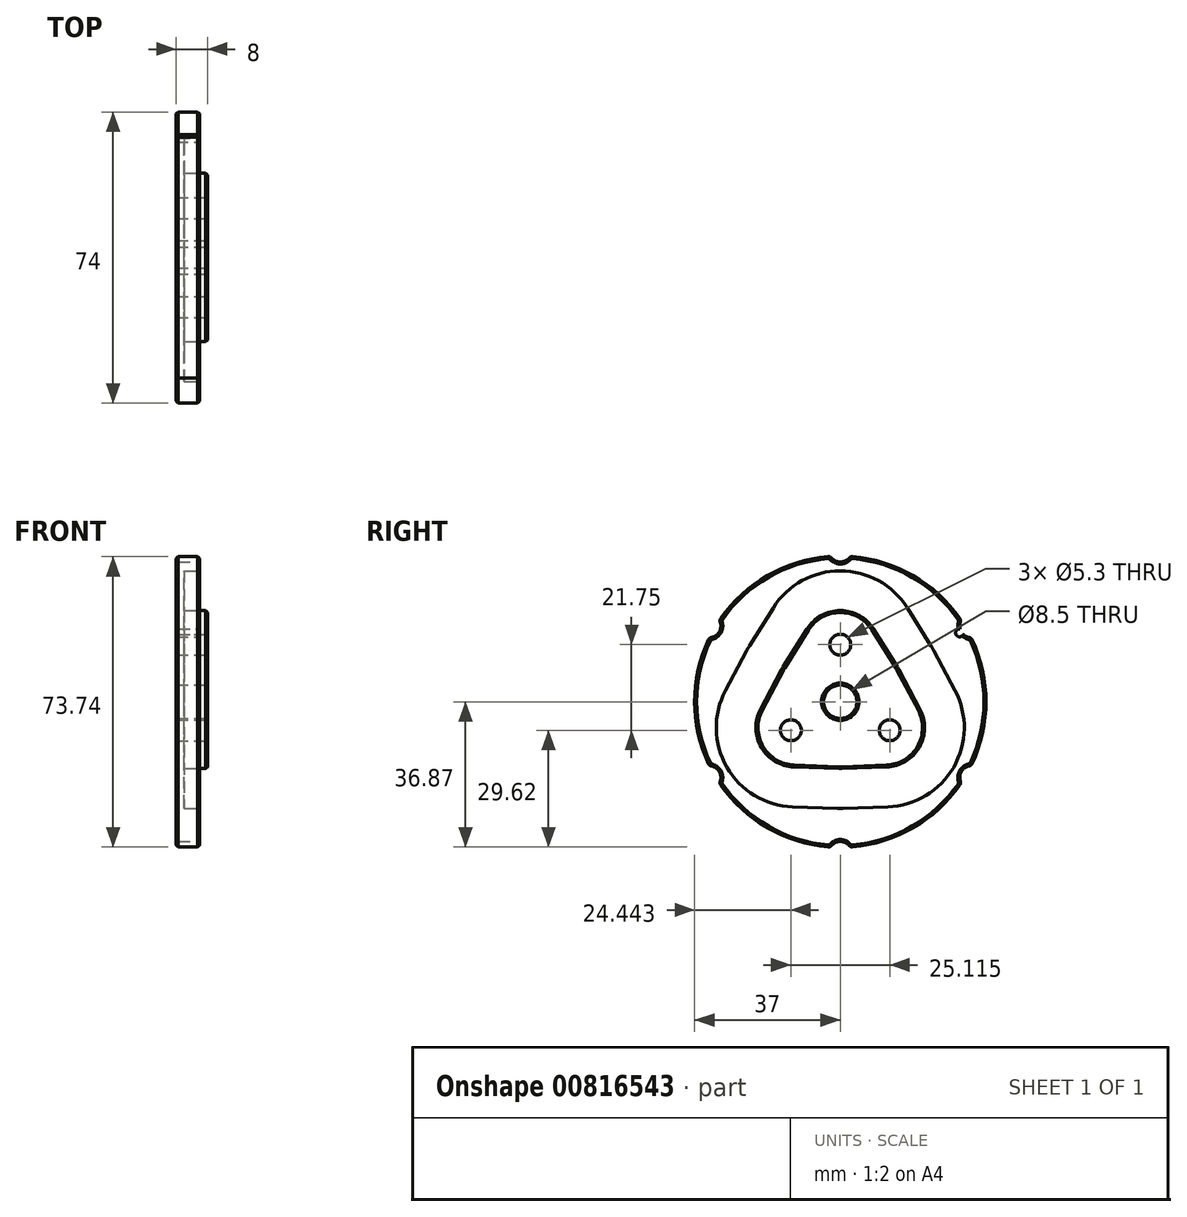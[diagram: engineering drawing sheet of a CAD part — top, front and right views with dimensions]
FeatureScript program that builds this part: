
annotation { "Feature Type Name" : "Feature", "Feature Type Description" : "" }
export const myFeature = defineFeature(function(context is Context, id is Id, definition is map)
    precondition{}
    {
        {
            var Q0;
            Q0=qCreatedBy(makeId("Right.planeOp"),FACE);
            var sketch = newSketch(context, id + "F0", { "sketchPlane" : qUnion([Q0])});
            skArc(sketch, "E0", {"start": v(-3.09, 36.87) * mm, "mid": v(-18.5, 32.04) * mm, "end": v(-30.39, 21.1) * mm});
            skCircle(sketch, "E1", {"center": v(0, 0) * mm, "radius": 4.25 * mm});
            skLineSegment(sketch, "E2", {"start": v(0, 50.53) * mm, "end": v(0, -45.3) * mm, "construction": true});
            skLineSegment(sketch, "E3", {"start": v(0, 0) * mm, "end": v(28.08, 48.64) * mm, "construction": true});
            skLineSegment(sketch, "E4", {"start": v(0, 0) * mm, "end": v(48.73, -28.13) * mm, "construction": true});
            skLineSegment(sketch, "E5.MirrorCS", {"start": v(0, 0) * mm, "end": v(-28.08, 48.64) * mm, "construction": true});
            skLineSegment(sketch, "E6.MirrorCS", {"start": v(-43.76, 25.27) * mm, "end": v(32.04, -18.5) * mm, "construction": true});
            skLineSegment(sketch, "E7.MirrorCS", {"start": v(0, 0) * mm, "end": v(-28.08, -48.64) * mm, "construction": true});
            skLineSegment(sketch, "E8.MirrorCS", {"start": v(0, 0) * mm, "end": v(28.08, -48.64) * mm, "construction": true});
            skLineSegment(sketch, "E9", {"start": v(-8.48, 18.48) * mm, "end": v(-14.54, 8.81) * mm});
            skLineSegment(sketch, "E10", {"start": v(-14.9, 8.18) * mm, "end": v(-20.25, -1.9) * mm});
            skLineSegment(sketch, "E11", {"start": v(-11.78, -16.58) * mm, "end": v(-0.36, -17) * mm});
            skLineSegment(sketch, "E12", {"start": v(0.36, -17) * mm, "end": v(11.77, -16.58) * mm});
            skLineSegment(sketch, "E13", {"start": v(20.24, -1.9) * mm, "end": v(14.9, 8.18) * mm});
            skLineSegment(sketch, "E14", {"start": v(14.53, 8.8) * mm, "end": v(8.47, 18.48) * mm});
            skPoint(sketch, "E15.visualSharp", {"position": v(0, 32) * mm});
            skArc(sketch, "E15.filletArc", {"start": v(8.47, 18.48) * mm, "mid": v(0, 23.17) * mm, "end": v(-8.48, 18.48) * mm});
            skPoint(sketch, "E16.visualSharp", {"position": v(-14.73, 8.5) * mm});
            skArc(sketch, "E16.filletArc", {"start": v(-14.54, 8.81) * mm, "mid": v(-14.73, 8.5) * mm, "end": v(-14.9, 8.18) * mm});
            skPoint(sketch, "E17.visualSharp", {"position": v(-27.71, -16) * mm});
            skArc(sketch, "E17.filletArc", {"start": v(-20.25, -1.9) * mm, "mid": v(-20.07, -11.59) * mm, "end": v(-11.78, -16.58) * mm});
            skPoint(sketch, "E18.visualSharp", {"position": v(0, -17.01) * mm});
            skArc(sketch, "E18.filletArc", {"start": v(-0.36, -17) * mm, "mid": v(0, -17) * mm, "end": v(0.36, -17) * mm});
            skPoint(sketch, "E19.visualSharp", {"position": v(27.71, -16) * mm});
            skArc(sketch, "E19.filletArc", {"start": v(11.77, -16.58) * mm, "mid": v(20.07, -11.59) * mm, "end": v(20.24, -1.9) * mm});
            skPoint(sketch, "E20.visualSharp", {"position": v(14.72, 8.5) * mm});
            skArc(sketch, "E20.filletArc", {"start": v(14.9, 8.18) * mm, "mid": v(14.72, 8.5) * mm, "end": v(14.53, 8.8) * mm});
            skLineSegment(sketch, "E21.0", {"start": v(-17.03, 23.85) * mm, "end": v(-23.1, 14.18) * mm});
            skArc(sketch, "E21.1", {"start": v(-0.73, -27.1) * mm, "mid": v(0, -27.1) * mm, "end": v(0.73, -27.1) * mm});
            skLineSegment(sketch, "E21.2", {"start": v(-12.14, -26.67) * mm, "end": v(-0.73, -27.1) * mm});
            skArc(sketch, "E21.3", {"start": v(-29.17, 2.82) * mm, "mid": v(-28.82, -16.64) * mm, "end": v(-12.14, -26.67) * mm});
            skLineSegment(sketch, "E21.4", {"start": v(-23.83, 12.91) * mm, "end": v(-29.17, 2.82) * mm});
            skLineSegment(sketch, "E21.5", {"start": v(0.73, -27.1) * mm, "end": v(12.14, -26.68) * mm});
            skArc(sketch, "E21.6", {"start": v(-23.1, 14.18) * mm, "mid": v(-23.47, 13.55) * mm, "end": v(-23.83, 12.91) * mm});
            skArc(sketch, "E21.7", {"start": v(12.14, -26.68) * mm, "mid": v(28.81, -16.63) * mm, "end": v(29.16, 2.83) * mm});
            skLineSegment(sketch, "E21.8", {"start": v(29.16, 2.83) * mm, "end": v(23.81, 12.91) * mm});
            skArc(sketch, "E21.9", {"start": v(23.81, 12.91) * mm, "mid": v(23.46, 13.55) * mm, "end": v(23.09, 14.17) * mm});
            skLineSegment(sketch, "E21.10", {"start": v(23.09, 14.17) * mm, "end": v(17.03, 23.84) * mm});
            skArc(sketch, "E21.11", {"start": v(17.03, 23.84) * mm, "mid": v(0, 33.27) * mm, "end": v(-17.03, 23.85) * mm});
            skCircle(sketch, "E22", {"center": v(0, 0) * mm, "radius": 14.5 * mm, "construction": true});
            skCircle(sketch, "E23", {"center": v(-12.56, -7.25) * mm, "radius": 2.65 * mm});
            skCircle(sketch, "E24", {"center": v(12.56, -7.25) * mm, "radius": 2.65 * mm});
            skCircle(sketch, "E25", {"center": v(0, 14.5) * mm, "radius": 2.65 * mm});
            skArc(sketch, "E26", {"start": v(30.45, 18.5) * mm, "mid": v(29.44, 17) * mm, "end": v(31.24, 17.13) * mm});
            skArc(sketch, "E27", {"start": v(-2.25, 36.53) * mm, "mid": v(0, 35.5) * mm, "end": v(2.25, 36.53) * mm});
            skPoint(sketch, "E28.visualSharp", {"position": v(-2.53, 36.91) * mm});
            skArc(sketch, "E28.filletArc", {"start": v(-2.25, 36.53) * mm, "mid": v(-2.63, 36.8) * mm, "end": v(-3.09, 36.87) * mm});
            skPoint(sketch, "E29.visualSharp", {"position": v(2.53, 36.91) * mm});
            skArc(sketch, "E29.filletArc", {"start": v(3.09, 36.87) * mm, "mid": v(2.63, 36.8) * mm, "end": v(2.25, 36.53) * mm});
            skPoint(sketch, "E30.center.orphan", {"position": v(0, -35) * mm});
            skArc(sketch, "E31.MirrorCS", {"start": v(32.76, 16.32) * mm, "mid": v(33.19, 16.12) * mm, "end": v(33.48, 15.76) * mm});
            skArc(sketch, "E32.MirrorCS", {"start": v(30.39, 21.1) * mm, "mid": v(30.56, 20.68) * mm, "end": v(30.51, 20.22) * mm});
            skPoint(sketch, "E33.MirrorP", {"position": v(33.23, 16.26) * mm});
            skArc(sketch, "E34.MirrorCS", {"start": v(32.76, 16.32) * mm, "mid": v(31.94, 16.6) * mm, "end": v(31.24, 17.13) * mm});
            skPoint(sketch, "E35.MirrorP", {"position": v(30.7, 20.65) * mm});
            skArc(sketch, "E36.trimOffspring", {"start": v(30.39, 21.1) * mm, "mid": v(18.5, 32.04) * mm, "end": v(3.09, 36.87) * mm});
            skLineSegment(sketch, "E37.trimOffspring", {"start": v(31.18, 18) * mm, "end": v(-39.22, -22.65) * mm, "construction": true});
            skArc(sketch, "E38.trimOffspring", {"start": v(30.45, 18.5) * mm, "mid": v(30.35, 19.36) * mm, "end": v(30.51, 20.22) * mm});
            skArc(sketch, "E39.MirrorCS", {"start": v(-30.51, 20.22) * mm, "mid": v(-30.56, 20.68) * mm, "end": v(-30.39, 21.1) * mm});
            skArc(sketch, "E40.MirrorCS", {"start": v(-33.48, 15.76) * mm, "mid": v(-33.19, 16.12) * mm, "end": v(-32.76, 16.32) * mm});
            skPoint(sketch, "E41.MirrorP", {"position": v(-33.23, 16.26) * mm});
            skPoint(sketch, "E42.MirrorP", {"position": v(-30.7, 20.65) * mm});
            skArc(sketch, "E43.MirrorCS", {"start": v(-30.51, 20.22) * mm, "mid": v(-30.75, 17.75) * mm, "end": v(-32.76, 16.32) * mm});
            skArc(sketch, "E44.trimOffspring", {"start": v(-33.48, 15.76) * mm, "mid": v(-37, 0) * mm, "end": v(-33.48, -15.76) * mm});
            skArc(sketch, "E45.MirrorCS", {"start": v(-33.48, -15.76) * mm, "mid": v(-33.19, -16.12) * mm, "end": v(-32.76, -16.32) * mm});
            skArc(sketch, "E46.MirrorCS", {"start": v(-30.51, -20.22) * mm, "mid": v(-30.56, -20.68) * mm, "end": v(-30.39, -21.1) * mm});
            skPoint(sketch, "E47.MirrorP", {"position": v(-30.7, -20.65) * mm});
            skArc(sketch, "E48.MirrorCS", {"start": v(-30.51, -20.22) * mm, "mid": v(-30.75, -17.75) * mm, "end": v(-32.76, -16.32) * mm});
            skPoint(sketch, "E49.MirrorP", {"position": v(-33.23, -16.26) * mm});
            skArc(sketch, "E50.trimOffspring", {"start": v(-30.39, -21.1) * mm, "mid": v(-18.5, -32.04) * mm, "end": v(-3.09, -36.87) * mm});
            skArc(sketch, "E51.MirrorCS", {"start": v(3.09, -36.87) * mm, "mid": v(2.63, -36.8) * mm, "end": v(2.25, -36.53) * mm});
            skArc(sketch, "E52.MirrorCS", {"start": v(-2.25, -36.53) * mm, "mid": v(-2.63, -36.8) * mm, "end": v(-3.09, -36.87) * mm});
            skArc(sketch, "E53.MirrorCS", {"start": v(-2.25, -36.53) * mm, "mid": v(0, -35.5) * mm, "end": v(2.25, -36.53) * mm});
            skPoint(sketch, "E54.MirrorP", {"position": v(-2.53, -36.91) * mm});
            skPoint(sketch, "E55.MirrorP", {"position": v(2.53, -36.91) * mm});
            skArc(sketch, "E56.trimOffspring", {"start": v(3.09, -36.87) * mm, "mid": v(18.5, -32.04) * mm, "end": v(30.39, -21.1) * mm});
            skPoint(sketch, "E57.orphan", {"position": v(39.22, -22.65) * mm});
            skPoint(sketch, "E58.MirrorCS.start.orphan", {"position": v(43.76, 25.27) * mm});
            skArc(sketch, "E59.MirrorCS", {"start": v(30.39, -21.1) * mm, "mid": v(30.56, -20.68) * mm, "end": v(30.51, -20.22) * mm});
            skArc(sketch, "E60.MirrorCS", {"start": v(32.76, -16.32) * mm, "mid": v(33.19, -16.12) * mm, "end": v(33.48, -15.76) * mm});
            skPoint(sketch, "E61.MirrorP", {"position": v(33.23, -16.26) * mm});
            skPoint(sketch, "E62.MirrorP", {"position": v(30.7, -20.65) * mm});
            skPoint(sketch, "E63.MirrorP", {"position": v(30.31, -17.5) * mm});
            skArc(sketch, "E64.MirrorCS", {"start": v(32.76, -16.32) * mm, "mid": v(30.75, -17.75) * mm, "end": v(30.51, -20.22) * mm});
            skArc(sketch, "E65.trimOffspring", {"start": v(33.48, -15.76) * mm, "mid": v(37, 0) * mm, "end": v(33.48, 15.76) * mm});
            skSolve(sketch);
        }
        {
            var Q0;
            Q0 = qSketchRegion(id + "F0", true);
            var Q1;
            Q1=makeQuery(id+"F0.imprint","IMPRINT",FACE,{"disambiguationData":[TD([[makeQuery(id+"F0.imprint","IMPRINT",EDGE,{"derivedFrom":sQuery(id+"F0.wireOp",EDGE,"E9")}),-1.0]])]});
            var Q2;
            Q2=makeQuery(id+"F0.imprint","IMPRINT",FACE,{"disambiguationData":[TD([[makeQuery(id+"F0.imprint","IMPRINT",EDGE,{"derivedFrom":sQuery(id+"F0.wireOp",EDGE,"E1")}),-1.0]])]});
            extrude(context, id + "F1", {"entities" : qUnion([Q0, Q1, Q2]), "oppositeDirection" : true, "depth" : 6 * mm, "offsetDistance" : 25 * mm});
        }
        {
            var Q0;
            Q0=makeQuery(id+"F0.imprint","IMPRINT",FACE,{"disambiguationData":[TD([[makeQuery(id+"F0.imprint","IMPRINT",EDGE,{"derivedFrom":sQuery(id+"F0.wireOp",EDGE,"E9")}),-1.0]])]});
            extrude(context, id + "F2", {"entities" : qUnion([Q0]), "operationType" : NewBodyOperationType.REMOVE, "oppositeDirection" : true, "depth" : 4 * mm, "offsetDistance" : 25 * mm});
        }
        {
            var Q0;
            {var subQ0=sQuery(id+"F0.wireOp",EDGE,"E1");Q0=makeQuery(id+"F2.boolean.opBoolean","SPLIT",FACE,{"disambiguationData":[TD([makeQuery(id+"F1.opExtrude","SWEPT_FACE",FACE,{"disambiguationData":[OSD([subQ0])]})])],"derivedFrom":makeQuery(id+"F1.opExtrude","CAP_FACE",FACE,{"disambiguationData":[OSD([sQuery(id+"F0.wireOp",EDGE,"E0"),subQ0])],"isStart":true})});}
            extrude(context, id + "F3", {"entities" : qUnion([Q0]), "operationType" : NewBodyOperationType.ADD, "depth" : 2 * mm, "offsetDistance" : 25 * mm});
        }
        {
            var Q0;
            Q0=makeQuery(id+"FyIsF6kSJw19HWJ_1.boolean.opBoolean","COPY",EDGE,{"derivedFrom":makeQuery(id+"FyIsF6kSJw19HWJ_1.opExtrude","CAP_EDGE",EDGE,{"disambiguationData":[OSD([sQuery(id+"F7LV2Zl85KT3uEW_1.wireOp",EDGE,"4heGY6iT-OKOq-OImW-84Io-U2CDUhAUHW4h")])],"isStart":true})});
            var Q1;
            Q1=makeQuery(id+"F1.opExtrude","CAP_EDGE",EDGE,{"disambiguationData":[OSD([sQuery(id+"F0.wireOp",EDGE,"E56.trimOffspring")])],"isStart":false});
            var Q2;
            Q2=makeQuery(id+"F1.opExtrude","CAP_EDGE",EDGE,{"disambiguationData":[OSD([sQuery(id+"F0.wireOp",EDGE,"E56.trimOffspring")])],"isStart":true});
            var Q3;
            Q3=makeQuery(id+"F2.boolean.opBoolean","COPY",EDGE,{"derivedFrom":makeQuery(id+"F2.opExtrude","CAP_EDGE",EDGE,{"disambiguationData":[OSD([sQuery(id+"F0.wireOp",EDGE,"E21.7")])],"isStart":true})});
            var Q4;
            Q4=makeQuery(id+"F3.opExtrude","CAP_EDGE",EDGE,{"disambiguationData":[OSD([sQuery(id+"F0.wireOp",EDGE,"E19.filletArc")])],"isStart":false});
            var Q5;
            Q5=makeQuery(id+"F3.opExtrude","CAP_EDGE",EDGE,{"disambiguationData":[OSD([sQuery(id+"F0.wireOp",EDGE,"E1")])],"isStart":false});
            var Q6;
            Q6=makeQuery(id+"FyIsF6kSJw19HWJ_1.boolean.opBoolean","COPY",EDGE,{"derivedFrom":makeQuery(id+"FyIsF6kSJw19HWJ_1.opExtrude","CAP_EDGE",EDGE,{"disambiguationData":[OSD([sQuery(id+"F0.wireOp",EDGE,"E1")])],"isStart":false})});
            chamfer(context, id + "F4", {"entities" : qUnion([Q0, Q1, Q2, Q3, Q4, Q5, Q6]), "width" : 0.5 * mm, "tangentPropagation" : true});
        }
    });
